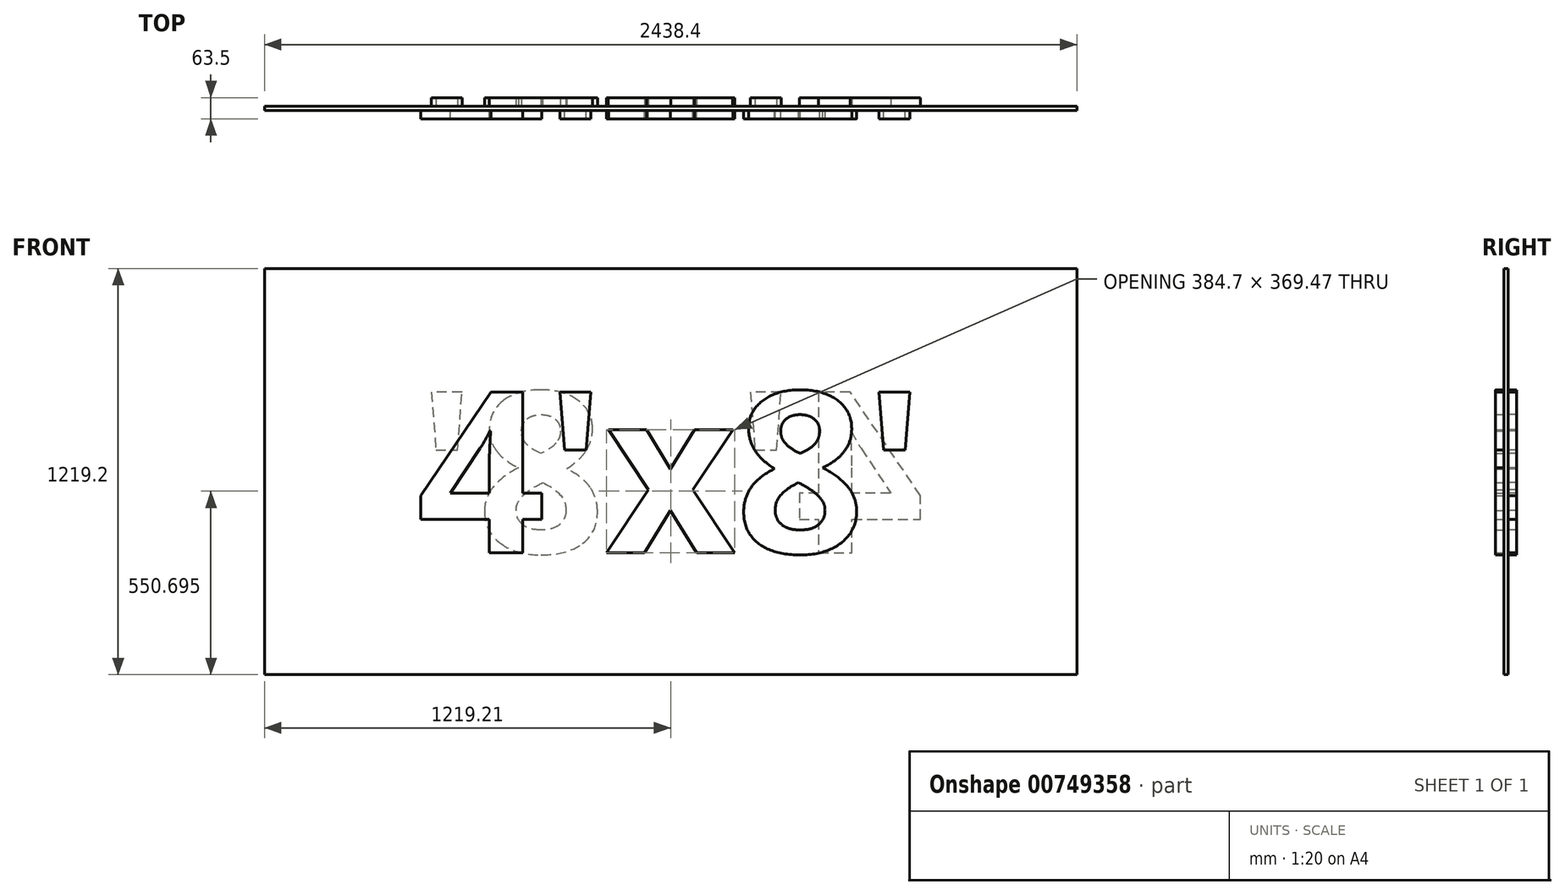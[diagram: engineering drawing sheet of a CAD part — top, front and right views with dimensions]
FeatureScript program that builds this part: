
annotation { "Feature Type Name" : "Feature", "Feature Type Description" : "" }
export const myFeature = defineFeature(function(context is Context, id is Id, definition is map)
    precondition{}
    {
        {
            var Q0;
            Q0=qCreatedBy(makeId("Front.planeOp"),FACE);
            var sketch = newSketch(context, id + "F0", { "sketchPlane" : qUnion([Q0])});
            skLineSegment(sketch, "E0.bottom", {"start": v(0, 0) * mm, "end": v(2438.4, 0) * mm});
            skLineSegment(sketch, "E0.top", {"start": v(0, 1219.2) * mm, "end": v(2438.4, 1219.2) * mm});
            skLineSegment(sketch, "E0.left", {"start": v(0, 0) * mm, "end": v(0, 1219.2) * mm});
            skLineSegment(sketch, "E0.right", {"start": v(2438.4, 0) * mm, "end": v(2438.4, 1219.2) * mm});
            skSolve(sketch);
        }
        {
            var Q0;
            Q0=makeQuery(id+"F0.imprint","IMPRINT",FACE,{"disambiguationData":[TD([[makeQuery(id+"F0.imprint","IMPRINT",EDGE,{"derivedFrom":sQuery(id+"F0.wireOp",EDGE,"E0.bottom")}),1.0]])]});
            extrude(context, id + "F1", {"entities" : qUnion([Q0]), "depth" : 12.7 * mm, "offsetDistance" : 25.4 * mm});
        }
        {
            var Q0;
            Q0=makeQuery(id+"F1.opExtrude","CAP_FACE",FACE,{"disambiguationData":[OSD([sQuery(id+"F0.wireOp",EDGE,"E0.bottom"),sQuery(id+"F0.wireOp",EDGE,"E0.top"),sQuery(id+"F0.wireOp",EDGE,"E0.left"),sQuery(id+"F0.wireOp",EDGE,"E0.right")])],"isStart":false});
            var sketch = newSketch(context, id + "F2", { "sketchPlane" : qUnion([Q0])});
            skText(sketch, "E1", { "text": "4\'x8\'", "fontName": "OpenSans-Bold.ttf"});
            skPoint(sketch, "E2", {"position": v(457.2, 609.6) * mm});
            const initialGuessF2  = {"E1": [0.4572, 0.36596, 1, 0, 0.48727]};
            skSetInitialGuess(sketch, initialGuessF2);
            skSolve(sketch);
        }
        {
            var Q0;
            Q0=makeQuery(id+"F2.imprint","IMPRINT",FACE,{"disambiguationData":[TD([[makeQuery(id+"F2.imprint","IMPRINT",EDGE,{"derivedFrom":sQuery(id+"F2.wireOp",EDGE,"E1.sketch_text.stroke-0")}),-1.0]])]});
            var Q1;
            Q1=makeQuery(id+"F2.imprint","IMPRINT",FACE,{"disambiguationData":[TD([[makeQuery(id+"F2.imprint","IMPRINT",EDGE,{"derivedFrom":sQuery(id+"F2.wireOp",EDGE,"E1.sketch_text.stroke-18")}),-1.0]])]});
            var Q2;
            Q2=makeQuery(id+"F2.imprint","IMPRINT",FACE,{"disambiguationData":[TD([[makeQuery(id+"F2.imprint","IMPRINT",EDGE,{"derivedFrom":sQuery(id+"F2.wireOp",EDGE,"E1.sketch_text.stroke-22")}),-1.0]])]});
            var Q3;
            Q3=makeQuery(id+"F2.imprint","IMPRINT",FACE,{"disambiguationData":[TD([[makeQuery(id+"F2.imprint","IMPRINT",EDGE,{"derivedFrom":sQuery(id+"F2.wireOp",EDGE,"E1.sketch_text.stroke-34")}),-1.0]])]});
            var Q4;
            Q4=makeQuery(id+"F2.imprint","IMPRINT",FACE,{"disambiguationData":[TD([[makeQuery(id+"F2.imprint","IMPRINT",EDGE,{"derivedFrom":sQuery(id+"F2.wireOp",EDGE,"E1.sketch_text.stroke-65")}),-1.0]])]});
            extrude(context, id + "F3", {"entities" : qUnion([Q0, Q1, Q2, Q3, Q4]), "operationType" : NewBodyOperationType.ADD, "depth" : 25.4 * mm, "offsetDistance" : 25.4 * mm});
        }
        {
            var Q0;
            Q0=makeQuery(id+"F1.opExtrude","CAP_FACE",FACE,{"disambiguationData":[OSD([sQuery(id+"F0.wireOp",EDGE,"E0.bottom"),sQuery(id+"F0.wireOp",EDGE,"E0.top"),sQuery(id+"F0.wireOp",EDGE,"E0.left"),sQuery(id+"F0.wireOp",EDGE,"E0.right")])],"isStart":true});
            var sketch = newSketch(context, id + "F4", { "sketchPlane" : qUnion([Q0])});
            skText(sketch, "E3", { "text": "4\'x8\'", "fontName": "OpenSans-Bold.ttf"});
            skPoint(sketch, "E4", {"position": v(-1981.2, 609.6) * mm});
            const initialGuessF4  = {"E3": [-1.9812, 0.36596, 1, 0, 0.48727]};
            skSetInitialGuess(sketch, initialGuessF4);
            skSolve(sketch);
        }
        {
            var Q0;
            Q0=makeQuery(id+"F4.imprint","IMPRINT",FACE,{"disambiguationData":[TD([[makeQuery(id+"F4.imprint","IMPRINT",EDGE,{"derivedFrom":sQuery(id+"F4.wireOp",EDGE,"E3.sketch_text.stroke-22")}),-1.0]])]});
            var Q1;
            Q1=makeQuery(id+"F4.imprint","IMPRINT",FACE,{"disambiguationData":[TD([[makeQuery(id+"F4.imprint","IMPRINT",EDGE,{"derivedFrom":sQuery(id+"F4.wireOp",EDGE,"E3.sketch_text.stroke-34")}),-1.0]])]});
            var Q2;
            Q2=makeQuery(id+"F4.imprint","IMPRINT",FACE,{"disambiguationData":[TD([[makeQuery(id+"F4.imprint","IMPRINT",EDGE,{"derivedFrom":sQuery(id+"F4.wireOp",EDGE,"E3.sketch_text.stroke-65")}),-1.0]])]});
            var Q3;
            Q3=makeQuery(id+"F4.imprint","IMPRINT",FACE,{"disambiguationData":[TD([[makeQuery(id+"F4.imprint","IMPRINT",EDGE,{"derivedFrom":sQuery(id+"F4.wireOp",EDGE,"E3.sketch_text.stroke-18")}),-1.0]])]});
            var Q4;
            Q4=makeQuery(id+"F4.imprint","IMPRINT",FACE,{"disambiguationData":[TD([[makeQuery(id+"F4.imprint","IMPRINT",EDGE,{"derivedFrom":sQuery(id+"F4.wireOp",EDGE,"E3.sketch_text.stroke-0")}),-1.0]])]});
            extrude(context, id + "F5", {"entities" : qUnion([Q0, Q1, Q2, Q3, Q4]), "operationType" : NewBodyOperationType.ADD, "depth" : 25.4 * mm, "offsetDistance" : 25.4 * mm});
        }
    });
